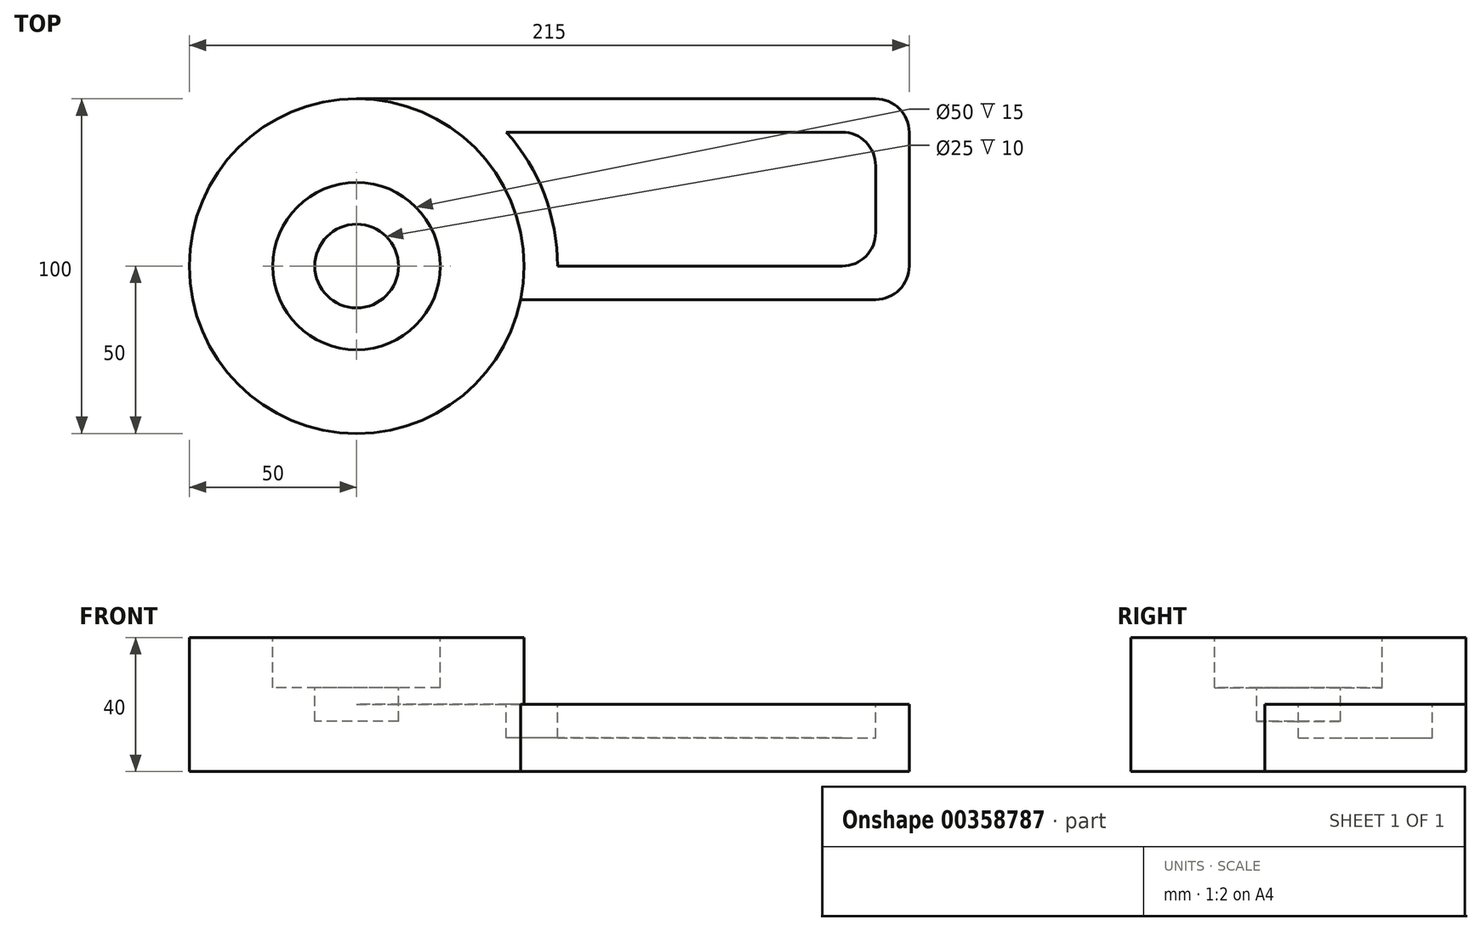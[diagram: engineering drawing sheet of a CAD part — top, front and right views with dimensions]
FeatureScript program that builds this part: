
annotation { "Feature Type Name" : "Feature", "Feature Type Description" : "" }
export const myFeature = defineFeature(function(context is Context, id is Id, definition is map)
    precondition{}
    {
        {
            var Q0;
            Q0=qCreatedBy(makeId("Top.planeOp"),FACE);
            var sketch = newSketch(context, id + "F0", { "sketchPlane" : qUnion([Q0])});
            skCircle(sketch, "E0", {"center": v(0, 0) * mm, "radius": 50 * mm});
            skLineSegment(sketch, "E1.bottom", {"start": v(0, 50) * mm, "end": v(165, 50) * mm});
            skLineSegment(sketch, "E1.top", {"start": v(0, -10) * mm, "end": v(165, -10) * mm});
            skLineSegment(sketch, "E1.left", {"start": v(0, 50) * mm, "end": v(0, -10) * mm});
            skLineSegment(sketch, "E1.right", {"start": v(165, 50) * mm, "end": v(165, -10) * mm});
            skSolve(sketch);
        }
        {
            var Q0;
            {var subQ0=sQuery(id+"F0.wireOp",EDGE,"E1.bottom");Q0=makeQuery(id+"F0.imprint","IMPRINT",FACE,{"disambiguationData":[TD([[makeQuery(id+"F0.imprint","IMPRINT",EDGE,{"derivedFrom":subQ0}),-1.0]])]});}
            extrude(context, id + "F1", {"entities" : qUnion([Q0]), "depth" : 20 * mm});
        }
        {
            var Q0;
            {var subQ0=sQuery(id+"F0.wireOp",EDGE,"E1.left");Q0=makeQuery(id+"F0.imprint","IMPRINT",FACE,{"disambiguationData":[TD([[makeQuery(id+"F0.imprint","IMPRINT",EDGE,{"derivedFrom":subQ0}),-1.0]])]});}
            var Q1;
            {var subQ0=sQuery(id+"F0.wireOp",EDGE,"E1.left");Q1=makeQuery(id+"F0.imprint","IMPRINT",FACE,{"disambiguationData":[TD([[makeQuery(id+"F0.imprint","IMPRINT",EDGE,{"derivedFrom":subQ0}),1.0]])]});}
            extrude(context, id + "F2", {"entities" : qUnion([Q0, Q1]), "operationType" : NewBodyOperationType.ADD, "depth" : 40 * mm});
        }
        {
            var Q0;
            Q0=makeQuery(id+"F2.opExtrude","CAP_FACE",FACE,{"disambiguationData":[OSD([sQuery(id+"F0.wireOp",EDGE,"E0")])],"isStart":false});
            var sketch = newSketch(context, id + "F3", { "sketchPlane" : qUnion([Q0])});
            skCircle(sketch, "E2", {"center": v(0, 0) * mm, "radius": 25 * mm});
            skSolve(sketch);
        }
        {
            var Q0;
            Q0 = qSketchRegion(id + "F3", true);
            extrude(context, id + "F4", {"entities" : qUnion([Q0]), "operationType" : NewBodyOperationType.REMOVE, "oppositeDirection" : true, "depth" : 15 * mm});
        }
        {
            var Q0;
            Q0=makeQuery(id+"F4.boolean.opBoolean","COPY",FACE,{"derivedFrom":makeQuery(id+"F4.opExtrude","CAP_FACE",FACE,{"disambiguationData":[OSD([sQuery(id+"F3.wireOp",EDGE,"E2")])],"isStart":false})});
            var sketch = newSketch(context, id + "F5", { "sketchPlane" : qUnion([Q0])});
            skCircle(sketch, "E3", {"center": v(0, 0) * mm, "radius": 12.5 * mm});
            skSolve(sketch);
        }
        {
            var Q0;
            Q0 = qSketchRegion(id + "F5", true);
            extrude(context, id + "F6", {"entities" : qUnion([Q0]), "operationType" : NewBodyOperationType.REMOVE, "oppositeDirection" : true, "depth" : 10 * mm});
        }
        {
            var Q0;
            Q0=makeQuery(id+"F1.opExtrude","CAP_FACE",FACE,{"disambiguationData":[OSD([sQuery(id+"F0.wireOp",EDGE,"E0"),sQuery(id+"F0.wireOp",EDGE,"E1.bottom"),sQuery(id+"F0.wireOp",EDGE,"E1.top"),sQuery(id+"F0.wireOp",EDGE,"E1.right")])],"isStart":false});
            var sketch = newSketch(context, id + "F7", { "sketchPlane" : qUnion([Q0])});
            skLineSegment(sketch, "E4.0", {"start": v(155, 40) * mm, "end": v(44.72, 40) * mm});
            skLineSegment(sketch, "E4.1", {"start": v(155, 0) * mm, "end": v(155, 40) * mm});
            skLineSegment(sketch, "E4.2", {"start": v(60, 0) * mm, "end": v(155, 0) * mm});
            skArc(sketch, "E4.3", {"start": v(44.72, 40) * mm, "mid": v(56.05, 21.4) * mm, "end": v(60, 0) * mm});
            skSolve(sketch);
        }
        {
            var Q0;
            Q0 = qSketchRegion(id + "F7", true);
            extrude(context, id + "F8", {"entities" : qUnion([Q0]), "operationType" : NewBodyOperationType.REMOVE, "oppositeDirection" : true, "depth" : 10 * mm});
        }
        {
            var Q0;
            Q0=makeQuery(id+"F1.opExtrude","SWEPT_EDGE",EDGE,{"disambiguationData":[OSD([sQuery(id+"F0.wireOp",EDGE,"E1.bottom"),sQuery(id+"F0.wireOp",EDGE,"E1.right")])]});
            var Q1;
            Q1=makeQuery(id+"F1.opExtrude","SWEPT_EDGE",EDGE,{"disambiguationData":[OSD([sQuery(id+"F0.wireOp",EDGE,"E1.top"),sQuery(id+"F0.wireOp",EDGE,"E1.right")])]});
            var Q2;
            Q2=makeQuery(id+"F8.boolean.opBoolean","COPY",EDGE,{"derivedFrom":makeQuery(id+"F8.opExtrude","SWEPT_EDGE",EDGE,{"disambiguationData":[OSD([sQuery(id+"F7.wireOp",EDGE,"E4.0"),sQuery(id+"F7.wireOp",EDGE,"E4.1")])]})});
            var Q3;
            Q3=makeQuery(id+"F8.boolean.opBoolean","COPY",EDGE,{"derivedFrom":makeQuery(id+"F8.opExtrude","SWEPT_EDGE",EDGE,{"disambiguationData":[OSD([sQuery(id+"F7.wireOp",EDGE,"E4.1"),sQuery(id+"F7.wireOp",EDGE,"E4.2")])]})});
            fillet(context, id + "F9", {"entities" : qUnion([Q0, Q1, Q2, Q3]), "radius" : 10 * mm, "tangentPropagation" : true, "allowEdgeOverflow" : false});
        }
    });
